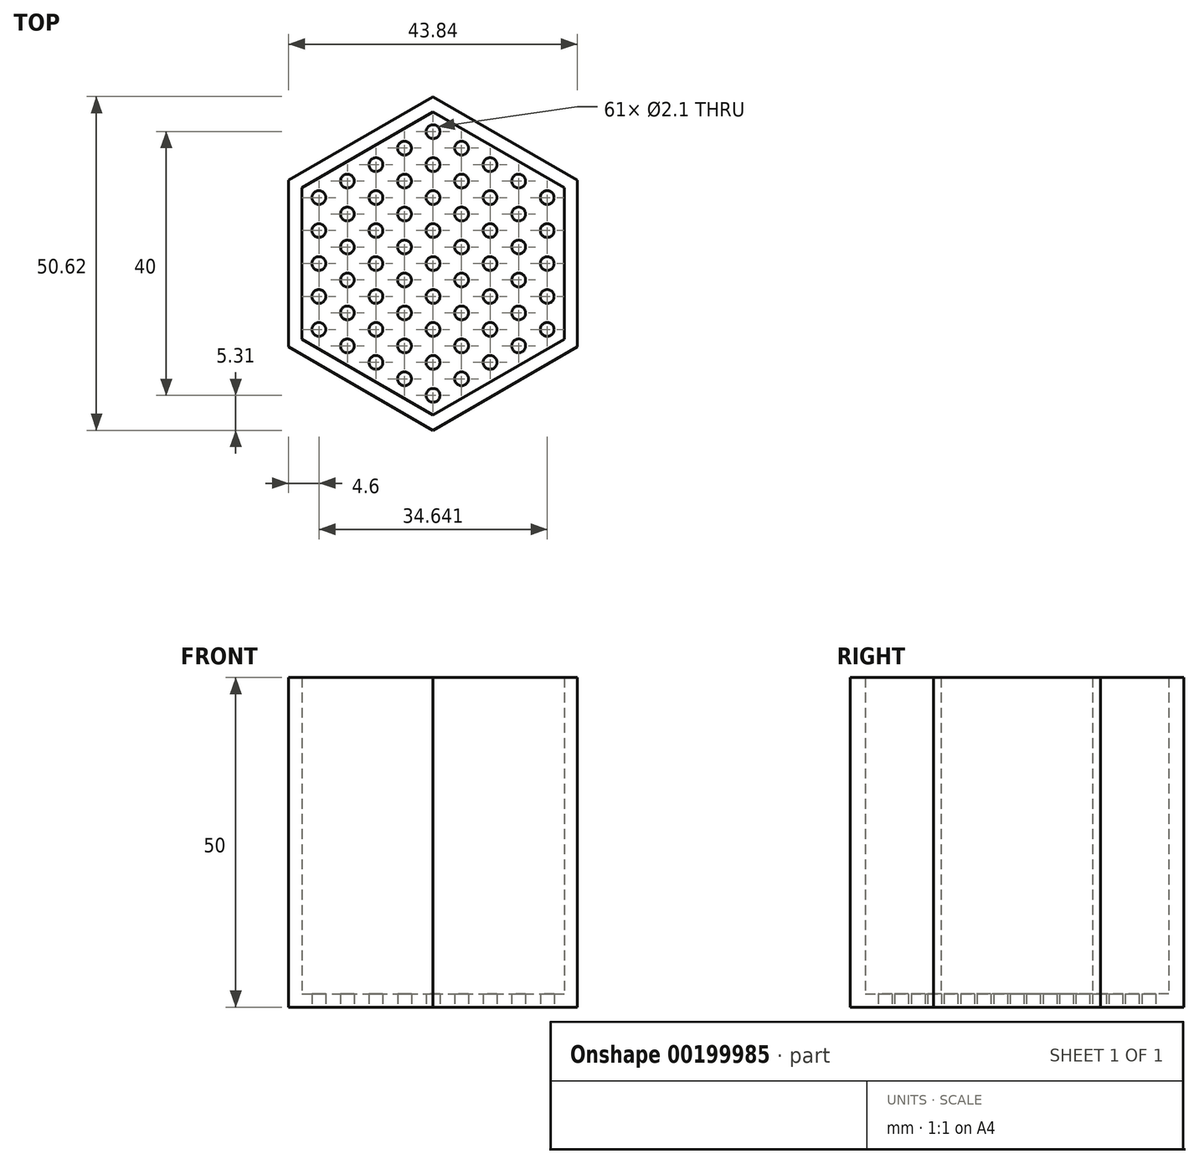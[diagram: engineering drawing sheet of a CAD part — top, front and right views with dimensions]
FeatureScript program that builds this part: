
annotation { "Feature Type Name" : "Feature", "Feature Type Description" : "" }
export const myFeature = defineFeature(function(context is Context, id is Id, definition is map)
    precondition{}
    {
        {
            var Q0;
            Q0=qCreatedBy(makeId("Top.planeOp"),FACE);
            var sketch = newSketch(context, id + "F0", { "sketchPlane" : qUnion([Q0])});
            skCircle(sketch, "E0.cCircle", {"center": v(0, 0) * mm, "radius": 23 * mm});
            skLineSegment(sketch, "E0.0", {"start": v(0, 23) * mm, "end": v(19.92, 11.5) * mm});
            skLineSegment(sketch, "E0.1", {"start": v(19.92, 11.5) * mm, "end": v(19.92, -11.5) * mm});
            skLineSegment(sketch, "E0.2", {"start": v(19.92, -11.5) * mm, "end": v(0, -23) * mm});
            skLineSegment(sketch, "E0.3", {"start": v(0, -23) * mm, "end": v(-19.92, -11.5) * mm});
            skLineSegment(sketch, "E0.4", {"start": v(-19.92, -11.5) * mm, "end": v(-19.92, 11.5) * mm});
            skLineSegment(sketch, "E0.5", {"start": v(-19.92, 11.5) * mm, "end": v(0, 23) * mm});
            skCircle(sketch, "E1", {"center": v(0, 0) * mm, "radius": 1.05 * mm});
            skLineSegment(sketch, "E2", {"start": v(-19.92, 11.5) * mm, "end": v(19.92, -11.5) * mm, "construction": true});
            skLineSegment(sketch, "E3", {"start": v(19.92, 11.5) * mm, "end": v(-19.92, -11.5) * mm, "construction": true});
            skLineSegment(sketch, "E4", {"start": v(0, 23) * mm, "end": v(0, -23) * mm, "construction": true});
            skCircle(sketch, "E5", {"center": v(0, 0) * mm, "radius": 2.5 * mm, "construction": true});
            skCircle(sketch, "E6", {"center": v(4.33, 2.5) * mm, "radius": 1.05 * mm});
            skCircle(sketch, "E7", {"center": v(8.66, 5) * mm, "radius": 1.05 * mm});
            skCircle(sketch, "E8", {"center": v(13, 7.5) * mm, "radius": 1.05 * mm});
            skCircle(sketch, "E9", {"center": v(17.32, 10) * mm, "radius": 1.05 * mm});
            skCircle(sketch, "E10", {"center": v(17.32, 10) * mm, "radius": 2.5 * mm, "construction": true});
            skCircle(sketch, "E11", {"center": v(0, 20) * mm, "radius": 1.05 * mm});
            skCircle(sketch, "E12", {"center": v(0, 15) * mm, "radius": 1.05 * mm});
            skCircle(sketch, "E13", {"center": v(0, 10) * mm, "radius": 1.05 * mm});
            skCircle(sketch, "E14", {"center": v(0, 5) * mm, "radius": 1.05 * mm});
            skLineSegment(sketch, "E15", {"start": v(-4.33, 2.5) * mm, "end": v(15.59, 14) * mm, "construction": true});
            skCircle(sketch, "E16", {"center": v(4.33, 7.5) * mm, "radius": 1.05 * mm});
            skCircle(sketch, "E17", {"center": v(8.66, 10) * mm, "radius": 1.05 * mm});
            skCircle(sketch, "E18", {"center": v(13, 12.5) * mm, "radius": 1.05 * mm});
            skLineSegment(sketch, "E19", {"start": v(-8.66, 5) * mm, "end": v(11.26, 16.5) * mm, "construction": true});
            skLineSegment(sketch, "E20", {"start": v(-13, 7.5) * mm, "end": v(6.93, 19) * mm, "construction": true});
            skLineSegment(sketch, "E21", {"start": v(-17.32, 10) * mm, "end": v(2.6, 21.5) * mm, "construction": true});
            skCircle(sketch, "E22", {"center": v(4.33, 12.5) * mm, "radius": 1.05 * mm});
            skCircle(sketch, "E23", {"center": v(8.66, 15) * mm, "radius": 1.05 * mm});
            skCircle(sketch, "E24", {"center": v(4.33, 17.5) * mm, "radius": 1.05 * mm});
            skLineSegment(sketch, "E25", {"start": v(0, 23) * mm, "end": v(0, 0) * mm});
            skLineSegment(sketch, "E26", {"start": v(0, 0) * mm, "end": v(19.92, 11.5) * mm});
            skLineSegment(sketch, "E27", {"start": v(0, 23) * mm, "end": v(0, 25.3) * mm});
            skLineSegment(sketch, "E28", {"start": v(0, 25.3) * mm, "end": v(21.92, 12.65) * mm});
            skLineSegment(sketch, "E29", {"start": v(21.92, 12.65) * mm, "end": v(19.92, 11.5) * mm});
            skSolve(sketch);
        }
        {
            var Q0;
            {var subQ5=sQuery(id+"F0.wireOp",EDGE,"E0.0");Q0=makeQuery(id+"F0.imprint","IMPRINT",FACE,{"disambiguationData":[TD([[makeQuery(id+"F0.imprint","IMPRINT",EDGE,{"derivedFrom":subQ5}),-1.0]])]});}
            var Q1;
            {var subQ0=sQuery(id+"F0.wireOp",EDGE,"E25");var subQ1=sQuery(id+"F0.wireOp",EDGE,"E1");var subQ2=makeQuery(id+"F0.imprint","INTERSECT",VERTEX,{"derivedFrom":[subQ1,subQ0]});Q1=makeQuery(id+"F0.imprint","IMPRINT",FACE,{"disambiguationData":[TD([[makeQuery(id+"F0.imprint","IMPRINT",EDGE,{"disambiguationData":[TD([[subQ2,1.0]])],"derivedFrom":subQ1}),1.0]])]});}
            extrude(context, id + "F1", {"entities" : qUnion([Q0, Q1]), "depth" : 2 * mm});
        }
        {
            var Q0;
            {var subQ0=sQuery(id+"F0.wireOp",EDGE,"E27");Q0=makeQuery(id+"F0.imprint","IMPRINT",FACE,{"disambiguationData":[TD([[makeQuery(id+"F0.imprint","IMPRINT",EDGE,{"derivedFrom":subQ0}),-1.0]])]});}
            var Q1;
            {var subQ0=sQuery(id+"F0.wireOp",EDGE,"E29");Q1=makeQuery(id+"F0.imprint","IMPRINT",FACE,{"disambiguationData":[TD([[makeQuery(id+"F0.imprint","IMPRINT",EDGE,{"derivedFrom":subQ0}),-1.0]])]});}
            var Q2;
            {var subQ0=sQuery(id+"F0.wireOp",EDGE,"E0.0");Q2=makeQuery(id+"F0.imprint","IMPRINT",FACE,{"disambiguationData":[TD([[makeQuery(id+"F0.imprint","IMPRINT",EDGE,{"derivedFrom":subQ0}),1.0]])]});}
            extrude(context, id + "F2", {"entities" : qUnion([Q0, Q1, Q2]), "operationType" : NewBodyOperationType.ADD, "depth" : 50 * mm});
        }
        {
            var Q0;
            Q0=makeQuery(id+"F1.opExtrude","SWEPT_BODY",BODY,{"disambiguationData":[OSD([sQuery(id+"F0.wireOp",EDGE,"E0.0"),sQuery(id+"F0.wireOp",EDGE,"E6"),sQuery(id+"F0.wireOp",EDGE,"E7"),sQuery(id+"F0.wireOp",EDGE,"E8"),sQuery(id+"F0.wireOp",EDGE,"E9"),sQuery(id+"F0.wireOp",EDGE,"E11"),sQuery(id+"F0.wireOp",EDGE,"E12"),sQuery(id+"F0.wireOp",EDGE,"E13"),sQuery(id+"F0.wireOp",EDGE,"E14"),sQuery(id+"F0.wireOp",EDGE,"E16"),sQuery(id+"F0.wireOp",EDGE,"E17"),sQuery(id+"F0.wireOp",EDGE,"E18"),sQuery(id+"F0.wireOp",EDGE,"E22"),sQuery(id+"F0.wireOp",EDGE,"E23"),sQuery(id+"F0.wireOp",EDGE,"E24"),sQuery(id+"F0.wireOp",EDGE,"E25"),sQuery(id+"F0.wireOp",EDGE,"E26")])]});
            var Q1;
            Q1=makeQuery(id+"F1.opExtrude","SWEPT_EDGE",EDGE,{"disambiguationData":[OSD([sQuery(id+"F0.wireOp",EDGE,"E25"),sQuery(id+"F0.wireOp",EDGE,"E26")])]});
            circularPattern(context, id + "F3", {"operationType" : NewBodyOperationType.ADD, "entities" : qUnion([Q0]), "axis" : qUnion([Q1]), "angle" : 360 * degree, "instanceCount" : 6, "equalSpace" : true});
        }
        {
            var Q0;
            {var subQ0=sQuery(id+"F0.wireOp",EDGE,"E25");var subQ1=sQuery(id+"F0.wireOp",EDGE,"E1");var subQ2=makeQuery(id+"F0.imprint","INTERSECT",VERTEX,{"derivedFrom":[subQ1,subQ0]});Q0=makeQuery(id+"F0.imprint","IMPRINT",FACE,{"disambiguationData":[TD([[makeQuery(id+"F0.imprint","IMPRINT",EDGE,{"disambiguationData":[TD([[subQ2,-1.0]])],"derivedFrom":subQ1}),1.0]])]});}
            var Q1;
            {var subQ0=sQuery(id+"F0.wireOp",EDGE,"E25");var subQ1=sQuery(id+"F0.wireOp",EDGE,"E1");var subQ2=makeQuery(id+"F0.imprint","INTERSECT",VERTEX,{"derivedFrom":[subQ1,subQ0]});Q1=makeQuery(id+"F0.imprint","IMPRINT",FACE,{"disambiguationData":[TD([[makeQuery(id+"F0.imprint","IMPRINT",EDGE,{"disambiguationData":[TD([[subQ2,1.0]])],"derivedFrom":subQ1}),1.0]])]});}
            extrude(context, id + "F4", {"entities" : qUnion([Q0, Q1]), "operationType" : NewBodyOperationType.REMOVE, "endBound" : BoundingType.THROUGH_ALL, "depth" : 25 * mm});
        }
    });
